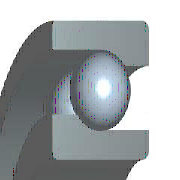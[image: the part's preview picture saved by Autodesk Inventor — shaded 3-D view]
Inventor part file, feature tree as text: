
AUTODESK INVENTOR PART (.ipt)
format: ipt  version: 2023.2 (Build 272271030, 271C)  size: 290,304 bytes
history: native  units: mm (DEFAULTED — no unit token found)
features: sketch x7, other x5, plane x3, fillet x2, pattern_circular x1
ambient origin geometry x8: Origin, YZ Plane, XZ Plane, XY Plane, X Axis, Y Axis, Z Axis, Center Point
bodies: Solid1 (feature_tree)
feature tree (18):
  plane  "WorkPlane1"
  plane  "Work Plane2"
  plane  "WorkPlane2"
  sketch  "Sketch1"  dims[d0=-15.0mm]
  other  "WorkPoint1"
  sketch  "Sketch2"  dims[d1=10.0mm]
  other  "WorkPoint3"
  sketch  "Sketch3"  dims[d2=10.0mm]
  other  "WorkPoint2"
  other  "WorkAxis1"
  sketch  "Sketch7"  dims[d6=15.0mm d7=360.0deg d8=7.0mm d9=7.5mm d10=8.1mm d11=9.6mm d12=360.0deg d13=4.05mm d14=4.8mm d15=360.0deg d16=60.0mm d18=360.0deg d19=0.6mm d20=1.1mm d21=36.0mm d22=30.24mm d23=41.76mm d26=0.0mm d27=0.0mm d28=0.0mm d29=0.0mm d30=0.0mm]
  other  "Work Axis2"
  pattern_circular  "PolarArray1"  Angle=360.0deg  [1 undecoded]
  fillet  "Fillet1"  Radius=7.0mm
  fillet  "Fillet2"  Radius=7.5mm
  sketch  "Sketch4"  dims[d3=23.5mm]
  sketch  "Sketch5"  dims[d4=26.0mm]
  sketch  "Sketch6"  dims[d5=14.0mm]
note: 1 required parameter value undecoded (feature->parameter linkage not recoverable at this tier; creation-order binding heuristic only, values carry confidence <= 0.55)
